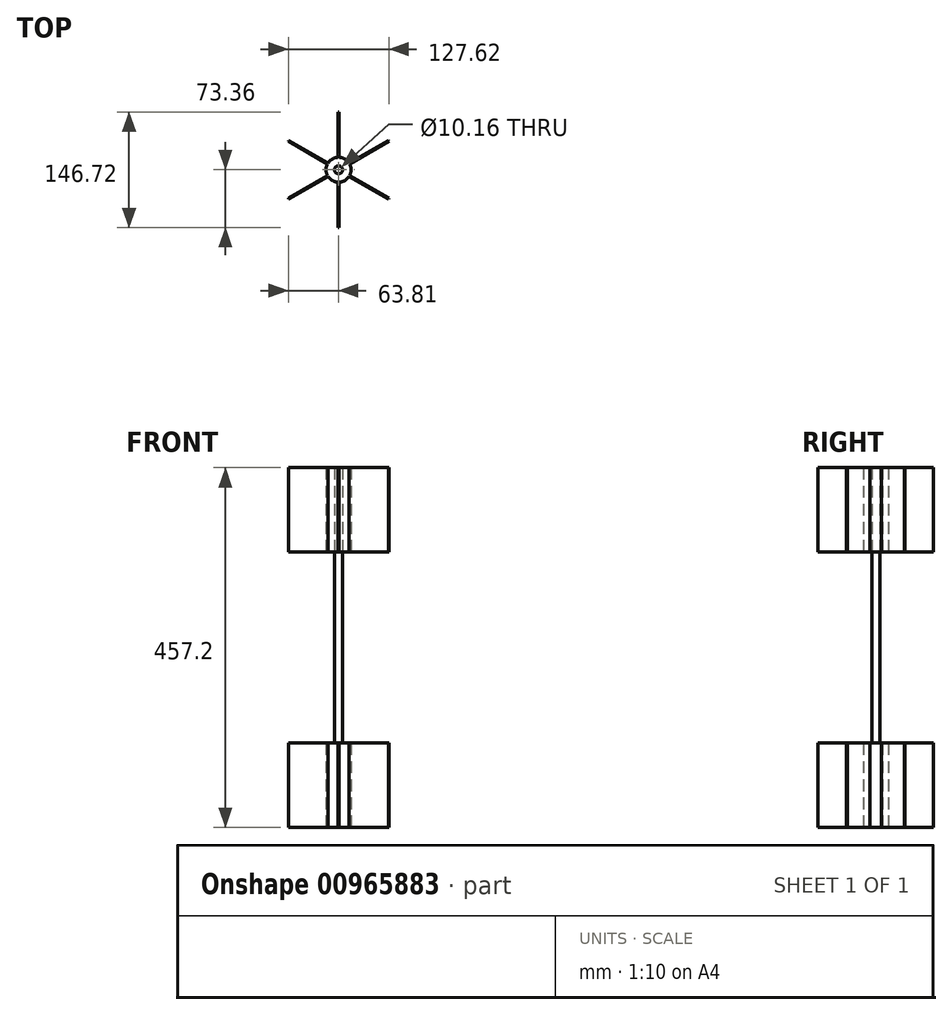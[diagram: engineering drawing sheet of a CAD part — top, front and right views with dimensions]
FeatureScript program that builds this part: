
annotation { "Feature Type Name" : "Feature", "Feature Type Description" : "" }
export const myFeature = defineFeature(function(context is Context, id is Id, definition is map)
    precondition{}
    {
        {
            var Q0;
            Q0=qCreatedBy(makeId("Top.planeOp"),FACE);
            var sketch = newSketch(context, id + "F0", { "sketchPlane" : qUnion([Q0])});
            skCircle(sketch, "E0", {"center": v(0, 0) * mm, "radius": 5.08 * mm});
            skArc(sketch, "E1", {"start": v(0.56, -15.87) * mm, "mid": v(7.94, -13.75) * mm, "end": v(13.46, -8.42) * mm});
            skCircle(sketch, "E2.cCircle", {"center": v(0, 0) * mm, "radius": 0.97 * mm, "construction": true});
            skLineSegment(sketch, "E2.0", {"start": v(0.56, -0.97) * mm, "end": v(-0.56, -0.97) * mm, "construction": true});
            skLineSegment(sketch, "E2.1", {"start": v(-0.56, -0.97) * mm, "end": v(-1.12, 0) * mm, "construction": true});
            skLineSegment(sketch, "E2.2", {"start": v(-1.12, 0) * mm, "end": v(-0.56, 0.97) * mm, "construction": true});
            skLineSegment(sketch, "E2.3", {"start": v(-0.56, 0.97) * mm, "end": v(0.56, 0.97) * mm, "construction": true});
            skLineSegment(sketch, "E2.4", {"start": v(0.56, 0.97) * mm, "end": v(1.12, 0) * mm, "construction": true});
            skLineSegment(sketch, "E2.5", {"start": v(1.12, 0) * mm, "end": v(0.56, -0.97) * mm, "construction": true});
            skPoint(sketch, "E2.0.midPoint", {"position": v(0, -0.97) * mm});
            skLineSegment(sketch, "E3.bottom", {"start": v(0.56, -0.97) * mm, "end": v(-0.56, -0.97) * mm});
            skLineSegment(sketch, "E3.top", {"start": v(0.56, -73.36) * mm, "end": v(-0.56, -73.36) * mm});
            skLineSegment(sketch, "E3.left", {"start": v(0.56, -0.97) * mm, "end": v(0.56, -5.05) * mm});
            skLineSegment(sketch, "E3.right", {"start": v(-0.56, -0.97) * mm, "end": v(-0.56, -5.05) * mm});
            skLineSegment(sketch, "E4.trimOffspring", {"start": v(0.56, -15.87) * mm, "end": v(0.56, -73.36) * mm});
            skLineSegment(sketch, "E5.trimOffspring", {"start": v(-0.56, -15.87) * mm, "end": v(-0.56, -73.36) * mm});
            skLineSegment(sketch, "E6.1.0", {"start": v(63.8, -36.2) * mm, "end": v(63.25, -37.16) * mm});
            skLineSegment(sketch, "E6.1.1", {"start": v(13.46, -8.42) * mm, "end": v(63.25, -37.16) * mm});
            skLineSegment(sketch, "E6.1.2", {"start": v(14.02, -7.45) * mm, "end": v(63.8, -36.2) * mm});
            skLineSegment(sketch, "E6.2.0", {"start": v(63.25, 37.16) * mm, "end": v(63.8, 36.2) * mm});
            skLineSegment(sketch, "E6.2.1", {"start": v(14.02, 7.45) * mm, "end": v(63.8, 36.2) * mm});
            skLineSegment(sketch, "E6.2.2", {"start": v(13.46, 8.42) * mm, "end": v(63.25, 37.16) * mm});
            skLineSegment(sketch, "E6.3.0", {"start": v(-0.56, 73.36) * mm, "end": v(0.56, 73.36) * mm});
            skLineSegment(sketch, "E6.3.1", {"start": v(0.56, 15.87) * mm, "end": v(0.56, 73.36) * mm});
            skLineSegment(sketch, "E6.3.2", {"start": v(-0.56, 15.87) * mm, "end": v(-0.56, 73.36) * mm});
            skLineSegment(sketch, "E6.4.0", {"start": v(-63.8, 36.2) * mm, "end": v(-63.25, 37.16) * mm});
            skLineSegment(sketch, "E6.4.1", {"start": v(-13.46, 8.42) * mm, "end": v(-63.25, 37.16) * mm});
            skLineSegment(sketch, "E6.4.2", {"start": v(-14.02, 7.45) * mm, "end": v(-63.8, 36.2) * mm});
            skLineSegment(sketch, "E6.5.0", {"start": v(-63.25, -37.16) * mm, "end": v(-63.8, -36.2) * mm});
            skLineSegment(sketch, "E6.5.1", {"start": v(-14.02, -7.45) * mm, "end": v(-63.8, -36.2) * mm});
            skLineSegment(sketch, "E6.5.2", {"start": v(-13.46, -8.42) * mm, "end": v(-63.25, -37.16) * mm});
            skArc(sketch, "E7.trimOffspring", {"start": v(14.02, -7.45) * mm, "mid": v(15.88, 0) * mm, "end": v(14.02, 7.45) * mm});
            skArc(sketch, "E8.trimOffspring", {"start": v(13.46, 8.42) * mm, "mid": v(7.94, 13.75) * mm, "end": v(0.56, 15.87) * mm});
            skArc(sketch, "E9.trimOffspring", {"start": v(-13.46, -8.42) * mm, "mid": v(-7.94, -13.75) * mm, "end": v(-0.56, -15.87) * mm});
            skArc(sketch, "E10.trimOffspring", {"start": v(-14.02, 7.45) * mm, "mid": v(-15.88, 0) * mm, "end": v(-14.02, -7.45) * mm});
            skArc(sketch, "E11.trimOffspring", {"start": v(-0.56, 15.87) * mm, "mid": v(-7.94, 13.75) * mm, "end": v(-13.46, 8.42) * mm});
            skSolve(sketch);
        }
        {
            var Q0;
            Q0=qCreatedBy(makeId("Top.planeOp"),FACE);
            var sketch = newSketch(context, id + "F1", { "sketchPlane" : qUnion([Q0])});
            skLineSegment(sketch, "E12.bottom", {"start": v(127, -127) * mm, "end": v(-127, -127) * mm});
            skLineSegment(sketch, "E12.top", {"start": v(127, 127) * mm, "end": v(-127, 127) * mm});
            skLineSegment(sketch, "E12.left", {"start": v(127, -127) * mm, "end": v(127, 127) * mm});
            skLineSegment(sketch, "E12.right", {"start": v(-127, -127) * mm, "end": v(-127, 127) * mm});
            skPoint(sketch, "E12.middle", {"position": v(0, 0) * mm});
            skSolve(sketch);
        }
        {
            var Q0;
            Q0=makeQuery(id+"F1.imprint","IMPRINT",FACE,{"disambiguationData":[TD([[makeQuery(id+"F1.imprint","IMPRINT",EDGE,{"derivedFrom":sQuery(id+"F1.wireOp",EDGE,"E12.bottom")}),-1.0]])]});
            extrude(context, id + "F2", {"entities" : qUnion([Q0]), "depth" : 107.19 * mm, "offsetDistance" : 25.4 * mm});
        }
        {
            var Q0;
            Q0=makeQuery(id+"F2.opExtrude","CAP_FACE",FACE,{"disambiguationData":[OSD([sQuery(id+"F1.wireOp",EDGE,"E12.bottom"),sQuery(id+"F1.wireOp",EDGE,"E12.top"),sQuery(id+"F1.wireOp",EDGE,"E12.left"),sQuery(id+"F1.wireOp",EDGE,"E12.right")])],"isStart":false});
            var sketch = newSketch(context, id + "F3", { "sketchPlane" : qUnion([Q0])});
            skCircle(sketch, "E13", {"center": v(0, 0) * mm, "radius": 5.08 * mm});
            skSolve(sketch);
        }
        {
            var Q0;
            Q0=makeQuery(id+"F3.imprint","IMPRINT",FACE,{"disambiguationData":[TD([[makeQuery(id+"F3.imprint","IMPRINT",EDGE,{"derivedFrom":sQuery(id+"F3.wireOp",EDGE,"E13")}),1.0]])]});
            extrude(context, id + "F4", {"entities" : qUnion([Q0]), "operationType" : NewBodyOperationType.ADD, "depth" : 242.82 * mm, "offsetDistance" : 25.4 * mm});
        }
        {
            var Q0;
            Q0=makeQuery(id+"F4.opExtrude","CAP_FACE",FACE,{"disambiguationData":[OSD([sQuery(id+"F3.wireOp",EDGE,"E13")])],"isStart":false});
            var sketch = newSketch(context, id + "F5", { "sketchPlane" : qUnion([Q0])});
            skLineSegment(sketch, "E14.bottom", {"start": v(-127, 127) * mm, "end": v(127, 127) * mm});
            skLineSegment(sketch, "E14.top", {"start": v(-127, -127) * mm, "end": v(127, -127) * mm});
            skLineSegment(sketch, "E14.left", {"start": v(-127, 127) * mm, "end": v(-127, -127) * mm});
            skLineSegment(sketch, "E14.right", {"start": v(127, 127) * mm, "end": v(127, -127) * mm});
            skPoint(sketch, "E14.middle", {"position": v(0, 0) * mm});
            skSolve(sketch);
        }
        {
            var Q0;
            Q0=makeQuery(id+"F5.imprint","IMPRINT",FACE,{"disambiguationData":[TD([[makeQuery(id+"F5.imprint","IMPRINT",EDGE,{"derivedFrom":sQuery(id+"F5.wireOp",EDGE,"E14.bottom")}),-1.0]])]});
            extrude(context, id + "F6", {"entities" : qUnion([Q0]), "depth" : 107.19 * mm, "offsetDistance" : 25.4 * mm});
        }
        {
            var Q0;
            Q0=makeQuery(id+"F4.opExtrude","CAP_FACE",FACE,{"disambiguationData":[OSD([sQuery(id+"F3.wireOp",EDGE,"E13")])],"isStart":false});
            var sketch = newSketch(context, id + "F7", { "sketchPlane" : qUnion([Q0])});
            skCircle(sketch, "E15", {"center": v(0, 0) * mm, "radius": 5.08 * mm});
            skSolve(sketch);
        }
        {
            var Q0;
            Q0=makeQuery(id+"F7.imprint","IMPRINT",FACE,{"disambiguationData":[TD([[makeQuery(id+"F7.imprint","IMPRINT",EDGE,{"derivedFrom":sQuery(id+"F7.wireOp",EDGE,"E15")}),1.0]])]});
            extrude(context, id + "F8", {"entities" : qUnion([Q0]), "depth" : 107.19 * mm, "offsetDistance" : 25.4 * mm});
        }
        {
            var Q0;
            Q0=makeQuery(id+"F0.imprint","IMPRINT",FACE,{"disambiguationData":[TD([[makeQuery(id+"F0.imprint","IMPRINT",EDGE,{"derivedFrom":sQuery(id+"F0.wireOp",EDGE,"E1")}),1.0]])]});
            var Q1;
            Q1=makeQuery(id+"F0.imprint","IMPRINT",FACE,{"disambiguationData":[TD([[makeQuery(id+"F0.imprint","IMPRINT",EDGE,{"derivedFrom":sQuery(id+"F0.wireOp",EDGE,"E3.bottom")}),-1.0]])]});
            var Q2;
            Q2=makeQuery(id+"F0.imprint","IMPRINT",FACE,{"disambiguationData":[TD([[makeQuery(id+"F0.imprint","IMPRINT",EDGE,{"derivedFrom":sQuery(id+"F0.wireOp",EDGE,"E3.bottom")}),1.0]])]});
            extrude(context, id + "F9", {"entities" : qUnion([Q0, Q1, Q2]), "operationType" : NewBodyOperationType.INTERSECT, "depth" : 543.3 * mm, "offsetDistance" : 25.4 * mm});
        }
    });
